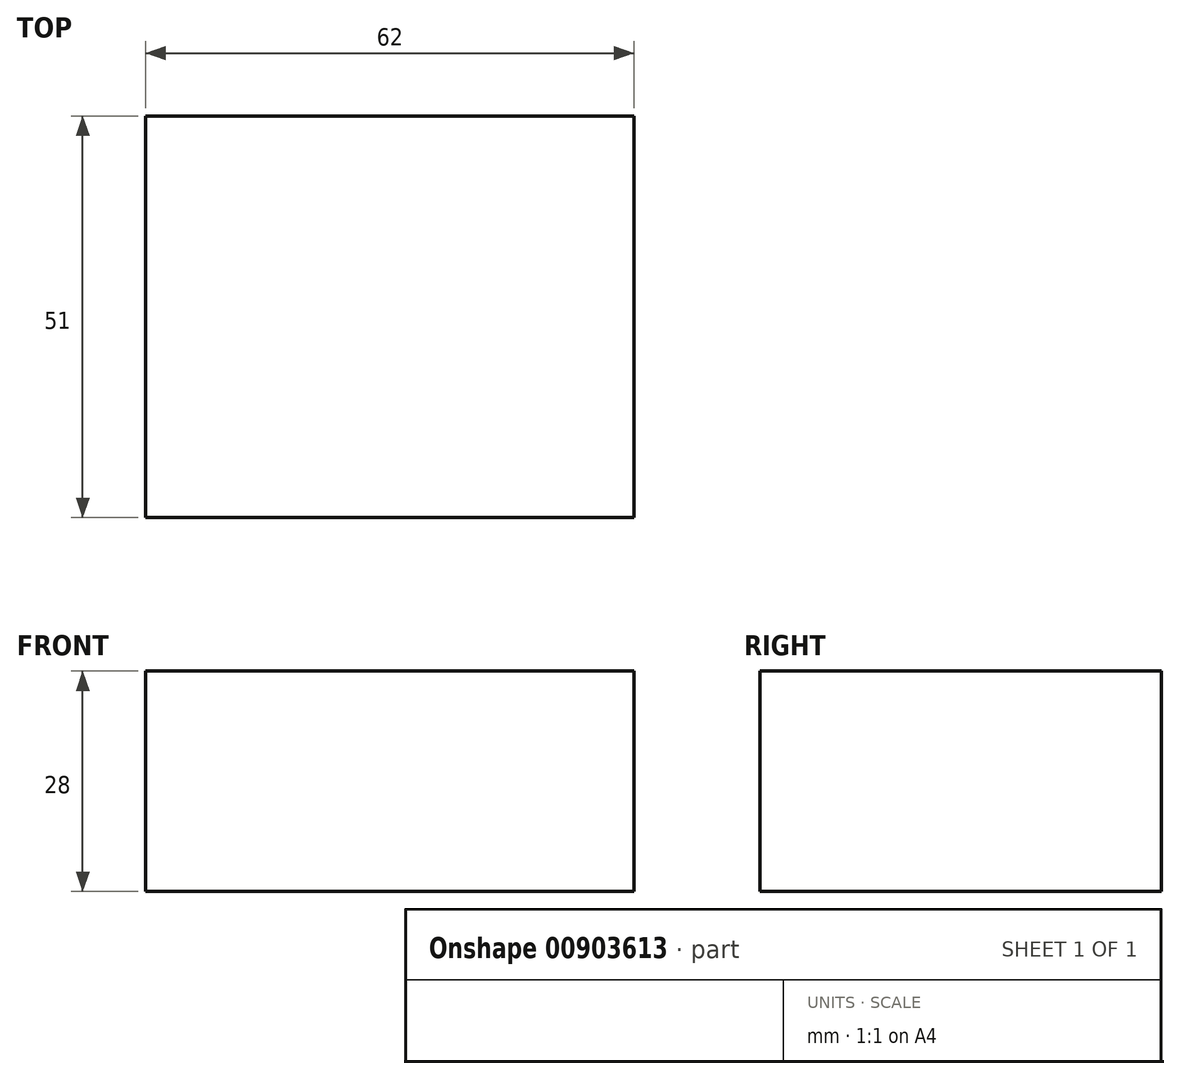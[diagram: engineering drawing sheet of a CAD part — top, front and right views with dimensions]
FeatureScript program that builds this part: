
annotation { "Feature Type Name" : "Feature", "Feature Type Description" : "" }
export const myFeature = defineFeature(function(context is Context, id is Id, definition is map)
    precondition{}
    {
        {
            var Q0;
            Q0=qCreatedBy(makeId("Top.planeOp"),FACE);
            var sketch = newSketch(context, id + "F0", { "sketchPlane" : qUnion([Q0])});
            skLineSegment(sketch, "E0.bottom", {"start": v(0, 0) * mm, "end": v(62, 0) * mm});
            skLineSegment(sketch, "E0.top", {"start": v(0, 51) * mm, "end": v(62, 51) * mm});
            skLineSegment(sketch, "E0.left", {"start": v(0, 0) * mm, "end": v(0, 51) * mm});
            skLineSegment(sketch, "E0.right", {"start": v(62, 0) * mm, "end": v(62, 51) * mm});
            skSolve(sketch);
        }
        {
            var Q0;
            Q0=qSketchRegion(id+"F0",true);
            extrude(context, id + "F1", {"entities" : qUnion([Q0]), "depth" : 28 * mm, "offsetDistance" : 25.4 * mm});
        }
    });
